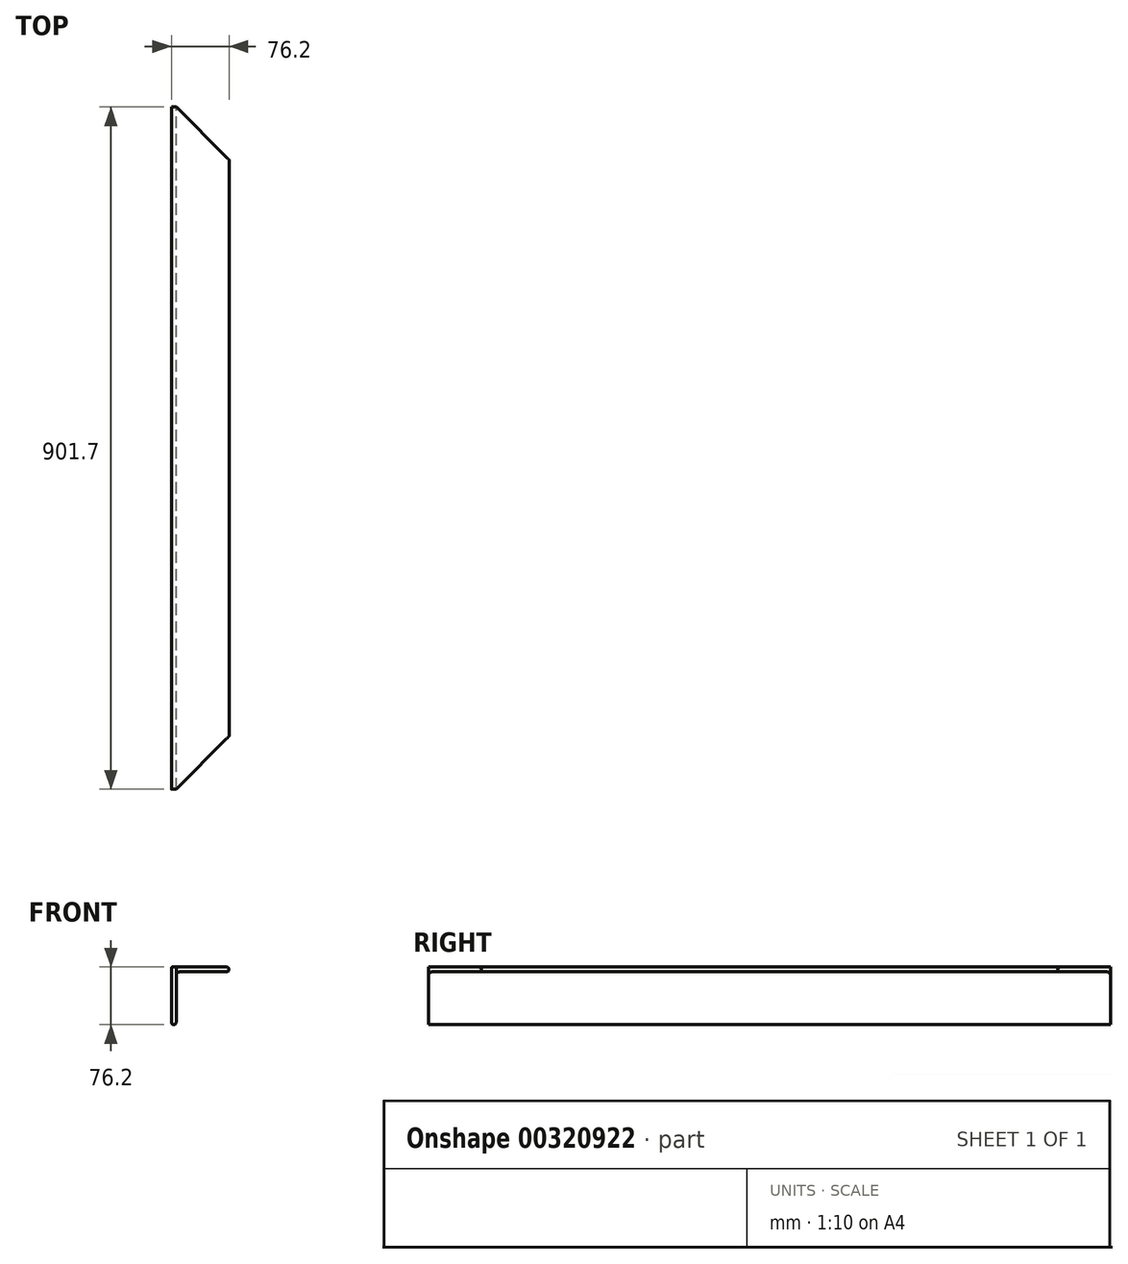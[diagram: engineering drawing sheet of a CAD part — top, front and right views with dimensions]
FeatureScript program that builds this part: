
annotation { "Feature Type Name" : "Feature", "Feature Type Description" : "" }
export const myFeature = defineFeature(function(context is Context, id is Id, definition is map)
    precondition{}
    {
        {
            var Q0;
            Q0=qCreatedBy(makeId("Front.planeOp"),FACE);
            var sketch = newSketch(context, id + "F0", { "sketchPlane" : qUnion([Q0])});
            skLineSegment(sketch, "E0", {"start": v(0, 0) * mm, "end": v(0, -76.2) * mm});
            skLineSegment(sketch, "E1", {"start": v(0, -76.2) * mm, "end": v(6.35, -76.2) * mm});
            skLineSegment(sketch, "E2", {"start": v(6.35, -76.2) * mm, "end": v(6.35, -6.35) * mm});
            skLineSegment(sketch, "E3", {"start": v(6.35, -6.35) * mm, "end": v(76.2, -6.35) * mm});
            skLineSegment(sketch, "E4", {"start": v(76.2, -6.35) * mm, "end": v(76.2, 0) * mm});
            skLineSegment(sketch, "E5", {"start": v(76.2, 0) * mm, "end": v(0, 0) * mm});
            skSolve(sketch);
        }
        {
            var Q0;
            Q0 = qSketchRegion(id + "F0", true);
            extrude(context, id + "F1", {"entities" : qUnion([Q0]), "endBound" : BoundingType.SYMMETRIC, "depth" : 901.7 * mm});
        }
        {
            var Q0;
            Q0=makeQuery(id+"F1.opExtrude","SWEPT_EDGE",EDGE,{"disambiguationData":[OSD([sQuery(id+"F0.wireOp",EDGE,"E2"),sQuery(id+"F0.wireOp",EDGE,"E3")])]});
            fillet(context, id + "F2", {"entities" : qUnion([Q0]), "radius" : 5.08 * mm, "tangentPropagation" : true, "allowEdgeOverflow" : false});
        }
        {
            var Q0;
            Q0=qCreatedBy(makeId("Top.planeOp"),FACE);
            var sketch = newSketch(context, id + "F3", { "sketchPlane" : qUnion([Q0])});
            skLineSegment(sketch, "E6.0.0", {"start": v(76.2, 450.85) * mm, "end": v(0, 450.85) * mm});
            skLineSegment(sketch, "E6.0.1", {"start": v(0, 450.85) * mm, "end": v(0, -450.85) * mm});
            skLineSegment(sketch, "E6.0.2", {"start": v(0, -450.85) * mm, "end": v(76.2, -450.85) * mm});
            skLineSegment(sketch, "E6.0.3", {"start": v(76.2, -450.85) * mm, "end": v(76.2, 450.85) * mm});
            skLineSegment(sketch, "E7", {"start": v(0, -450.85) * mm, "end": v(6.35, -450.85) * mm});
            skLineSegment(sketch, "E8", {"start": v(6.35, -450.85) * mm, "end": v(76.2, -381) * mm});
            skLineSegment(sketch, "E9", {"start": v(0, 450.85) * mm, "end": v(6.35, 450.85) * mm});
            skLineSegment(sketch, "E10", {"start": v(6.35, 450.85) * mm, "end": v(76.2, 381) * mm});
            skSolve(sketch);
        }
        {
            var Q0;
            {var subQ0=sQuery(id+"F3.wireOp",EDGE,"E6.0.0");Q0=makeQuery(id+"F3.imprint","IMPRINT",FACE,{"disambiguationData":[TD([[makeQuery(id+"F3.imprint","IMPRINT",EDGE,{"derivedFrom":subQ0}),1.0]])]});}
            var Q1;
            {var subQ0=sQuery(id+"F3.wireOp",EDGE,"E6.0.2");Q1=makeQuery(id+"F3.imprint","IMPRINT",FACE,{"disambiguationData":[TD([[makeQuery(id+"F3.imprint","IMPRINT",EDGE,{"derivedFrom":subQ0}),1.0]])]});}
            extrude(context, id + "F4", {"entities" : qUnion([Q0, Q1]), "operationType" : NewBodyOperationType.REMOVE, "endBound" : BoundingType.THROUGH_ALL, "oppositeDirection" : true, "depth" : 25.4 * mm});
        }
        {
            var Q0;
            Q0=makeQuery(id+"F1.opExtrude","SWEPT_EDGE",EDGE,{"disambiguationData":[OSD([sQuery(id+"F0.wireOp",EDGE,"E3"),sQuery(id+"F0.wireOp",EDGE,"E4")])]});
            var Q1;
            Q1=makeQuery(id+"F1.opExtrude","SWEPT_EDGE",EDGE,{"disambiguationData":[OSD([sQuery(id+"F0.wireOp",EDGE,"E4"),sQuery(id+"F0.wireOp",EDGE,"E5")])]});
            var Q2;
            Q2=makeQuery(id+"F1.opExtrude","SWEPT_EDGE",EDGE,{"disambiguationData":[OSD([sQuery(id+"F0.wireOp",EDGE,"E0"),sQuery(id+"F0.wireOp",EDGE,"E1")])]});
            var Q3;
            Q3=makeQuery(id+"F1.opExtrude","SWEPT_EDGE",EDGE,{"disambiguationData":[OSD([sQuery(id+"F0.wireOp",EDGE,"E1"),sQuery(id+"F0.wireOp",EDGE,"E2")])]});
            fillet(context, id + "F5", {"entities" : qUnion([Q0, Q1, Q2, Q3]), "radius" : 3.17 * mm, "tangentPropagation" : true, "allowEdgeOverflow" : false});
        }
        {
            var Q0;
            Q0=makeQuery(id+"F1.opExtrude","SWEPT_EDGE",EDGE,{"disambiguationData":[OSD([sQuery(id+"F0.wireOp",EDGE,"E0"),sQuery(id+"F0.wireOp",EDGE,"E5")])]});
            fillet(context, id + "F6", {"entities" : qUnion([Q0]), "radius" : 1.4 * mm, "tangentPropagation" : true, "allowEdgeOverflow" : false});
        }
    });
